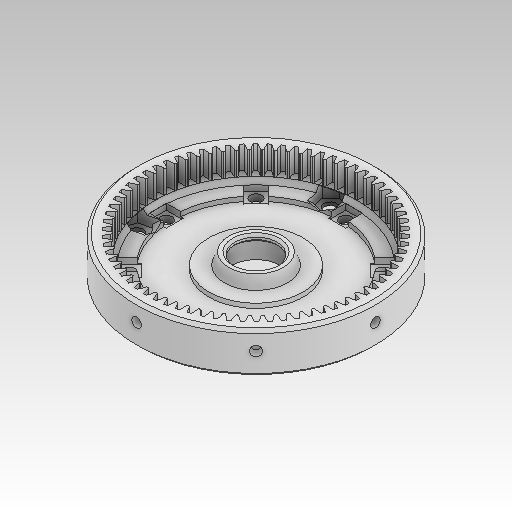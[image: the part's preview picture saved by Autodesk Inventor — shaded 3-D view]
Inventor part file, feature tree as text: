
AUTODESK INVENTOR PART (.ipt)
format: ipt  version: 2020 (Build 240168000, 168)  size: 1,923,072 bytes
history: native  units: mm
features: other x9, extrude x6, sketch x5, pattern_circular x4, chamfer x3, revolve x2, fillet x1, imported_body x1, projected_geometry x1
ambient origin geometry x8: Origin, YZ Plane, XZ Plane, XY Plane, X Axis, Y Axis, Z Axis, Center Point
bodies: Solid1 (feature_tree)
feature tree (32):
  other  "HD_mastersketch.ipt"
  other  "Blocks"
  revolve  "Revolution1"  [1 undecoded]
  extrude  "Extrusion1"  Depth=3.9mm
  extrude  "Extrusion3"  Depth=80.0mm TaperAngle=360.0deg
  pattern_circular  "Circular Pattern1"  [2 undecoded]
  extrude  "Extrusion2"  Depth=1.5mm
  fillet  "Fillet1"  Radius=700.0mm
  pattern_circular  "Circular Pattern2"  [2 undecoded]
  extrude  "Extrusion5"  Depth=1.5mm TaperAngle=0.0deg
  extrude  "Extrusion7"  Depth=1.5mm
  chamfer  "Chamfer1"  Distance=4.3mm
  extrude  "Extrusion8"  TaperAngle=0.0deg  [1 undecoded]
  chamfer  "Chamfer2"  Distance=2.268928mm
  pattern_circular  "Circular Pattern3"  [2 undecoded]
  revolve  "Revolution2"  [1 undecoded]
  pattern_circular  "Circular Pattern4"  Angle=45.0deg  [1 undecoded]
  chamfer  "Chamfer3"  Distance=8.726646mm
  other  "608 bearing"
  other  "Belt"
  other  "Rotor"
  imported_body  "Base"
  sketch  "Sketch5"  dims[d0=10.0mm d24=7.0mm d25=22.0mm d26=8.0mm]
  other  "M3NutDepth_bot"
  projected_geometry  "Projected Loop1"
  sketch  "Sketch7"  dims[d1=90.0deg d2=3.9mm]
  other  "BeltCutDepth_bot"
  sketch  "Sketch12"  dims[d4=4.0mm d5=0.0mm d6=80.0mm d7=360.0deg]
  sketch  "Sketch13"  dims[d9=0.8mm]
  sketch  "Sketch14"  dims[d11=1.8mm d12=4.0mm d13=0.0mm d14=0.45mm d15=700.0mm d16=360.0deg d18=5.7mm d19=4.0mm d20=0.0mm d29=47.0mm d30=4.3mm d31=0.0mm d32=0.0mm d38=2.268928mm d39=7.2mm d40=1.5mm d41=3.2mm d42=0.0mm d43=0.0mm d44=2.0mm d45=2.0mm d46=45.0deg d47=8.726646mm d48=0.523599mm d49=0.523599mm d50=0.523599mm d51=0.523599mm d52=0.523599mm d53=0.523599mm d56=2.792527mm d57=0.523599mm d58=68.0mm d59=70.740362mm d60=1.780032mm d61=9.749343mm d62=7.969311mm d63=6.189278mm d64=4.409246mm d65=2.629213mm d66=0.523599mm d67=0.523599mm d68=0.523599mm d69=0.523599mm d70=0.523599mm d72=11.529376mm d73=13.309408mm d74=15.089441mm d75=16.869473mm d76=18.649506mm d77=0.523599mm d78=0.523599mm d79=20.429538mm d80=22.209571mm d82=0.250579mm d83=72.932651mm d84=22.5mm d85=15.0mm d86=2.0mm d87=1.0mm d88=0.0mm d89=0.3mm d90=1.0mm d91=45.0deg d92=80.0mm d93=360.0deg d97=7.5mm d98=1.6mm d99=1.4mm d100=2.5mm d101=1.0mm d102=90.0deg d103=80.0mm d104=360.0deg d106=0.75mm d107=2.0mm d108=45.0deg]
  other  "608 bearing:1"
  other  "608 bearing:2"
note: 10 required parameter values undecoded (feature->parameter linkage not recoverable at this tier; creation-order binding heuristic only, values carry confidence <= 0.55)